# Revit family: REC-MP6T-2T21
name_source: partatom
category: Structural Connections
units: mm (PartAtom-declared; Revit-internal decimal feet)

## family parameters
Cut with Voids When Loaded = Yes
Enable Cutting in Views = Yes
Host = Face
Material for Model Behavior = Steel
Shared = No

## types (1)
- MP6T-2T21
    Classification.Uniclass.Pr.Description = Brackets
    Classification.Uniclass.Pr.Number = Pr_20_85_09
    Cost = 0 $
    Creado por: = Deliprogal SL
    Default Elevation = 0 mm  [stored 0 ft]
    Description = Pilar corbel 6 T,  with 2 holes Ø21 mm.
    Description_ESP = Ménsula de pilar 6 T, 2 taladros Ø21 mm.
    Export Type to IFC As = IfcElementAssembly
    Fecha Ultima Revision: = 01/03/2024
    Fecha de Creacion: = 01/03/2024
    IFCExportAs = IfcElementAssembly
    IFCExportType = Brackets
    Keynote = Supporting system for prefabricated panels on columns for loads up to 6T.
    Keynote_ESP = Sistema de sustentación de paneles prefabricados en pilares para cargas de hasta 6T.
    Manufacturer = RECENSE
    Model = MP6T-2T21
    Type IFC Predefined Type = Brackets
    URL = https://recense.com
    Visible = Yes

note: [stored X ft] marks values corroborated as IEEE doubles in the binary element streams (Revit-internal decimal feet)

## geometry (parser evidence)
native form markers: Sweep x3
no freeform markers — native parametric forms only
